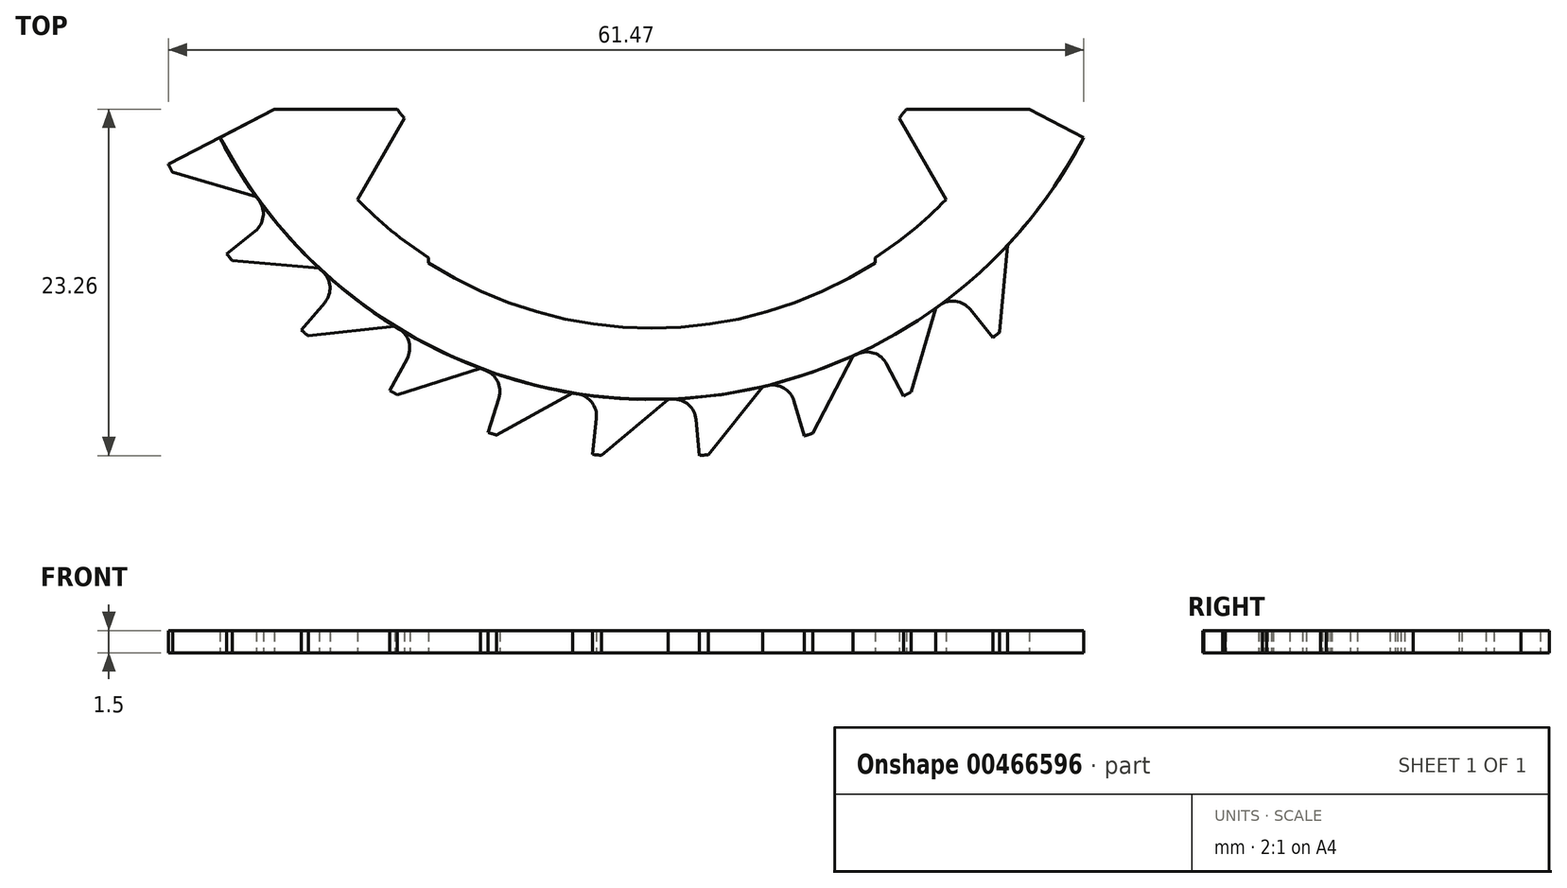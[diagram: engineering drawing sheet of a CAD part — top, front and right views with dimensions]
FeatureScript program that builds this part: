
annotation { "Feature Type Name" : "Feature", "Feature Type Description" : "" }
export const myFeature = defineFeature(function(context is Context, id is Id, definition is map)
    precondition{}
    {
        {
            var Q0;
            Q0=qCreatedBy(makeId("Top.planeOp"),FACE);
            var sketch = newSketch(context, id + "F0", { "sketchPlane" : qUnion([Q0])});
            skArc(sketch, "E0", {"start": v(5, -7.72) * mm, "mid": v(5.83, -7.12) * mm, "end": v(6.6, -6.42) * mm});
            skArc(sketch, "E1", {"start": v(-5, -7.84) * mm, "mid": v(0, -9.3) * mm, "end": v(5, -7.84) * mm});
            skArc(sketch, "E2", {"start": v(7.64, -9.51) * mm, "mid": v(7.71, -9.45) * mm, "end": v(7.8, -9.39) * mm});
            skCircle(sketch, "E3", {"center": v(0, 0) * mm, "radius": 10.9 * mm});
            skLineSegment(sketch, "E4", {"start": v(0, 0) * mm, "end": v(-10.82, -5.63) * mm});
            skLineSegment(sketch, "E5", {"start": v(0, 0) * mm, "end": v(9.67, -5.03) * mm});
            skLineSegment(sketch, "E6", {"start": v(0, 0) * mm, "end": v(7.64, -9.51) * mm, "construction": true});
            skLineSegment(sketch, "E7", {"start": v(6.82, -8.5) * mm, "end": v(7.64, -9.51) * mm});
            skLineSegment(sketch, "E8", {"start": v(7.8, -9.39) * mm, "end": v(7.96, -7.45) * mm});
            skLineSegment(sketch, "E9", {"start": v(0, 0) * mm, "end": v(9.35, -7.84) * mm, "construction": true});
            skLineSegment(sketch, "E10.1.0", {"start": v(5.8, -10.73) * mm, "end": v(6.36, -8.86) * mm});
            skArc(sketch, "E10.1.1", {"start": v(5.63, -10.82) * mm, "mid": v(5.72, -10.77) * mm, "end": v(5.8, -10.73) * mm});
            skLineSegment(sketch, "E10.1.2", {"start": v(5.03, -9.67) * mm, "end": v(5.63, -10.82) * mm});
            skLineSegment(sketch, "E10.2.0", {"start": v(3.6, -11.66) * mm, "end": v(4.5, -9.92) * mm});
            skArc(sketch, "E10.2.1", {"start": v(3.41, -11.71) * mm, "mid": v(3.5, -11.68) * mm, "end": v(3.6, -11.66) * mm});
            skLineSegment(sketch, "E10.2.2", {"start": v(3.05, -10.46) * mm, "end": v(3.41, -11.71) * mm});
            skLineSegment(sketch, "E10.3.0", {"start": v(1.26, -12.13) * mm, "end": v(2.48, -10.61) * mm});
            skArc(sketch, "E10.3.1", {"start": v(1.06, -12.15) * mm, "mid": v(1.16, -12.14) * mm, "end": v(1.26, -12.13) * mm});
            skLineSegment(sketch, "E10.3.2", {"start": v(0.95, -10.86) * mm, "end": v(1.06, -12.15) * mm});
            skLineSegment(sketch, "E10.4.0", {"start": v(-1.13, -12.15) * mm, "end": v(0.36, -10.9) * mm});
            skArc(sketch, "E10.4.1", {"start": v(-1.33, -12.13) * mm, "mid": v(-1.23, -12.14) * mm, "end": v(-1.13, -12.15) * mm});
            skLineSegment(sketch, "E10.4.2", {"start": v(-1.19, -10.84) * mm, "end": v(-1.33, -12.13) * mm});
            skLineSegment(sketch, "E10.5.0", {"start": v(-3.48, -11.7) * mm, "end": v(-1.77, -10.76) * mm});
            skArc(sketch, "E10.5.1", {"start": v(-3.67, -11.64) * mm, "mid": v(-3.57, -11.67) * mm, "end": v(-3.48, -11.7) * mm});
            skLineSegment(sketch, "E10.5.2", {"start": v(-3.28, -10.4) * mm, "end": v(-3.67, -11.64) * mm});
            skLineSegment(sketch, "E10.6.0", {"start": v(-5.7, -10.8) * mm, "end": v(-3.83, -10.2) * mm});
            skArc(sketch, "E10.6.1", {"start": v(-5.87, -10.7) * mm, "mid": v(-5.78, -10.74) * mm, "end": v(-5.7, -10.8) * mm});
            skLineSegment(sketch, "E10.6.2", {"start": v(-5.24, -9.56) * mm, "end": v(-5.87, -10.7) * mm});
            skLineSegment(sketch, "E10.7.0", {"start": v(-7.69, -9.47) * mm, "end": v(-5.75, -9.26) * mm});
            skArc(sketch, "E10.7.1", {"start": v(-7.84, -9.35) * mm, "mid": v(-7.77, -9.4) * mm, "end": v(-7.69, -9.47) * mm});
            skLineSegment(sketch, "E10.7.2", {"start": v(-7, -8.35) * mm, "end": v(-7.84, -9.35) * mm});
            skLineSegment(sketch, "E10.8.0", {"start": v(-9.39, -7.8) * mm, "end": v(-7.45, -7.96) * mm});
            skArc(sketch, "E10.8.1", {"start": v(-9.51, -7.64) * mm, "mid": v(-9.45, -7.71) * mm, "end": v(-9.39, -7.8) * mm});
            skLineSegment(sketch, "E10.8.2", {"start": v(-8.5, -6.82) * mm, "end": v(-9.51, -7.64) * mm});
            skLineSegment(sketch, "E10.9.0", {"start": v(-10.73, -5.8) * mm, "end": v(-8.86, -6.36) * mm});
            skArc(sketch, "E10.9.1", {"start": v(-10.82, -5.63) * mm, "mid": v(-10.77, -5.72) * mm, "end": v(-10.73, -5.8) * mm});
            skLineSegment(sketch, "E10.9.2", {"start": v(-9.67, -5.03) * mm, "end": v(-10.82, -5.63) * mm});
            skLineSegment(sketch, "E10.anchor1", {"start": v(0, 0) * mm, "end": v(7.8, -9.39) * mm, "construction": true});
            skLineSegment(sketch, "E10.anchor2", {"start": v(0, 0) * mm, "end": v(-9.58, -5.2) * mm, "construction": true});
            skArc(sketch, "E11", {"start": v(7.13, -8.88) * mm, "mid": v(6.8, -8.7) * mm, "end": v(6.44, -8.8) * mm});
            skArc(sketch, "E12.1.0", {"start": v(5.26, -10.1) * mm, "mid": v(4.98, -9.86) * mm, "end": v(4.6, -9.88) * mm});
            skArc(sketch, "E12.2.0", {"start": v(3.19, -10.93) * mm, "mid": v(2.96, -10.64) * mm, "end": v(2.59, -10.59) * mm});
            skArc(sketch, "E12.3.0", {"start": v(1, -11.35) * mm, "mid": v(0.82, -11.01) * mm, "end": v(0.47, -10.89) * mm});
            skArc(sketch, "E12.4.0", {"start": v(-1.24, -11.32) * mm, "mid": v(-1.34, -10.96) * mm, "end": v(-1.66, -10.77) * mm});
            skArc(sketch, "E12.5.0", {"start": v(-3.42, -10.86) * mm, "mid": v(-3.45, -10.5) * mm, "end": v(-3.73, -10.24) * mm});
            skArc(sketch, "E12.6.0", {"start": v(-5.48, -9.99) * mm, "mid": v(-5.43, -9.62) * mm, "end": v(-5.66, -9.32) * mm});
            skArc(sketch, "E12.7.0", {"start": v(-7.32, -8.72) * mm, "mid": v(-7.2, -8.37) * mm, "end": v(-7.37, -8.03) * mm});
            skArc(sketch, "E12.8.0", {"start": v(-8.88, -7.13) * mm, "mid": v(-8.7, -6.8) * mm, "end": v(-8.8, -6.44) * mm});
            skLineSegment(sketch, "E12.anchor1", {"start": v(6.44, -8.8) * mm, "end": v(0, 0) * mm, "construction": true});
            skLineSegment(sketch, "E12.anchor2", {"start": v(0, 0) * mm, "end": v(-8.8, -6.44) * mm, "construction": true});
            skCircle(sketch, "E13", {"center": v(0, 0) * mm, "radius": 12.2 * mm, "construction": true});
            skLineSegment(sketch, "E14", {"start": v(-8.45, -4.4) * mm, "end": v(-5.7, -4.4) * mm});
            skPoint(sketch, "E15", {"position": v(0, 5) * mm});
            skLineSegment(sketch, "E16", {"start": v(0, 5) * mm, "end": v(-6.6, -6.42) * mm});
            skLineSegment(sketch, "E17", {"start": v(0, 5) * mm, "end": v(6.6, -6.42) * mm});
            skLineSegment(sketch, "E18", {"start": v(-5, -7.72) * mm, "end": v(-5, -7.84) * mm});
            skLineSegment(sketch, "E19", {"start": v(5, -7.72) * mm, "end": v(5, -7.84) * mm});
            skArc(sketch, "E20.trimOffspring", {"start": v(5.52, -4.63) * mm, "mid": v(5.6, -4.51) * mm, "end": v(5.7, -4.4) * mm});
            skLineSegment(sketch, "E21.trimOffspring", {"start": v(5.7, -4.4) * mm, "end": v(8.45, -4.4) * mm});
            skLineSegment(sketch, "E22.trimOffspring", {"start": v(-9.58, -5.2) * mm, "end": v(-10.73, -5.8) * mm, "construction": true});
            skArc(sketch, "E23", {"start": v(-5.7, -4.4) * mm, "mid": v(-5.62, -4.5) * mm, "end": v(-5.54, -4.6) * mm});
            skArc(sketch, "E24", {"start": v(-6.6, -6.42) * mm, "mid": v(-5.83, -7.12) * mm, "end": v(-5, -7.72) * mm});
            skSolve(sketch);
        }
        {
            var Q0;
            {var subQ6=sQuery(id+"F0.wireOp",EDGE,"E0");Q0=makeQuery(id+"F0.imprint","IMPRINT",FACE,{"disambiguationData":[TD([[makeQuery(id+"F0.imprint","IMPRINT",EDGE,{"derivedFrom":subQ6}),-1.0]])]});}
            var Q1;
            {var subQ1=sQuery(id+"F0.wireOp",EDGE,"E10.9.0");Q1=makeQuery(id+"F0.imprint","IMPRINT",FACE,{"disambiguationData":[TD([[makeQuery(id+"F0.imprint","IMPRINT",EDGE,{"derivedFrom":subQ1}),1.0]])]});}
            var Q2;
            {var subQ5=sQuery(id+"F0.wireOp",EDGE,"E10.8.0");Q2=makeQuery(id+"F0.imprint","IMPRINT",FACE,{"disambiguationData":[TD([[makeQuery(id+"F0.imprint","IMPRINT",EDGE,{"derivedFrom":subQ5}),1.0]])]});}
            var Q3;
            {var subQ5=sQuery(id+"F0.wireOp",EDGE,"E10.7.0");Q3=makeQuery(id+"F0.imprint","IMPRINT",FACE,{"disambiguationData":[TD([[makeQuery(id+"F0.imprint","IMPRINT",EDGE,{"derivedFrom":subQ5}),1.0]])]});}
            var Q4;
            {var subQ5=sQuery(id+"F0.wireOp",EDGE,"E10.6.0");Q4=makeQuery(id+"F0.imprint","IMPRINT",FACE,{"disambiguationData":[TD([[makeQuery(id+"F0.imprint","IMPRINT",EDGE,{"derivedFrom":subQ5}),1.0]])]});}
            var Q5;
            {var subQ5=sQuery(id+"F0.wireOp",EDGE,"E10.5.0");Q5=makeQuery(id+"F0.imprint","IMPRINT",FACE,{"disambiguationData":[TD([[makeQuery(id+"F0.imprint","IMPRINT",EDGE,{"derivedFrom":subQ5}),1.0]])]});}
            var Q6;
            {var subQ5=sQuery(id+"F0.wireOp",EDGE,"E10.4.0");Q6=makeQuery(id+"F0.imprint","IMPRINT",FACE,{"disambiguationData":[TD([[makeQuery(id+"F0.imprint","IMPRINT",EDGE,{"derivedFrom":subQ5}),1.0]])]});}
            var Q7;
            {var subQ5=sQuery(id+"F0.wireOp",EDGE,"E10.3.0");Q7=makeQuery(id+"F0.imprint","IMPRINT",FACE,{"disambiguationData":[TD([[makeQuery(id+"F0.imprint","IMPRINT",EDGE,{"derivedFrom":subQ5}),1.0]])]});}
            var Q8;
            {var subQ2=sQuery(id+"F0.wireOp",EDGE,"E2");Q8=makeQuery(id+"F0.imprint","IMPRINT",FACE,{"disambiguationData":[TD([[makeQuery(id+"F0.imprint","IMPRINT",EDGE,{"derivedFrom":subQ2}),1.0]])]});}
            var Q9;
            {var subQ5=sQuery(id+"F0.wireOp",EDGE,"E10.1.0");Q9=makeQuery(id+"F0.imprint","IMPRINT",FACE,{"disambiguationData":[TD([[makeQuery(id+"F0.imprint","IMPRINT",EDGE,{"derivedFrom":subQ5}),1.0]])]});}
            var Q10;
            {var subQ5=sQuery(id+"F0.wireOp",EDGE,"E10.2.0");Q10=makeQuery(id+"F0.imprint","IMPRINT",FACE,{"disambiguationData":[TD([[makeQuery(id+"F0.imprint","IMPRINT",EDGE,{"derivedFrom":subQ5}),1.0]])]});}
            var Q11;
            {var subQ1=sQuery(id+"F0.wireOp",EDGE,"E11");Q11=makeQuery(id+"F0.imprint","IMPRINT",FACE,{"disambiguationData":[TD([[makeQuery(id+"F0.imprint","IMPRINT",EDGE,{"derivedFrom":subQ1}),-1.0]])]});}
            var Q12;
            {var subQ0=sQuery(id+"F0.wireOp",EDGE,"E12.1.0");Q12=makeQuery(id+"F0.imprint","IMPRINT",FACE,{"disambiguationData":[TD([[makeQuery(id+"F0.imprint","IMPRINT",EDGE,{"derivedFrom":subQ0}),-1.0]])]});}
            var Q13;
            {var subQ0=sQuery(id+"F0.wireOp",EDGE,"E12.2.0");Q13=makeQuery(id+"F0.imprint","IMPRINT",FACE,{"disambiguationData":[TD([[makeQuery(id+"F0.imprint","IMPRINT",EDGE,{"derivedFrom":subQ0}),-1.0]])]});}
            var Q14;
            {var subQ0=sQuery(id+"F0.wireOp",EDGE,"E12.3.0");Q14=makeQuery(id+"F0.imprint","IMPRINT",FACE,{"disambiguationData":[TD([[makeQuery(id+"F0.imprint","IMPRINT",EDGE,{"derivedFrom":subQ0}),-1.0]])]});}
            var Q15;
            {var subQ0=sQuery(id+"F0.wireOp",EDGE,"E12.4.0");Q15=makeQuery(id+"F0.imprint","IMPRINT",FACE,{"disambiguationData":[TD([[makeQuery(id+"F0.imprint","IMPRINT",EDGE,{"derivedFrom":subQ0}),-1.0]])]});}
            var Q16;
            {var subQ0=sQuery(id+"F0.wireOp",EDGE,"E12.5.0");Q16=makeQuery(id+"F0.imprint","IMPRINT",FACE,{"disambiguationData":[TD([[makeQuery(id+"F0.imprint","IMPRINT",EDGE,{"derivedFrom":subQ0}),-1.0]])]});}
            var Q17;
            {var subQ0=sQuery(id+"F0.wireOp",EDGE,"E12.6.0");Q17=makeQuery(id+"F0.imprint","IMPRINT",FACE,{"disambiguationData":[TD([[makeQuery(id+"F0.imprint","IMPRINT",EDGE,{"derivedFrom":subQ0}),-1.0]])]});}
            var Q18;
            {var subQ0=sQuery(id+"F0.wireOp",EDGE,"E12.8.0");Q18=makeQuery(id+"F0.imprint","IMPRINT",FACE,{"disambiguationData":[TD([[makeQuery(id+"F0.imprint","IMPRINT",EDGE,{"derivedFrom":subQ0}),-1.0]])]});}
            var Q19;
            {var subQ0=sQuery(id+"F0.wireOp",EDGE,"E12.7.0");Q19=makeQuery(id+"F0.imprint","IMPRINT",FACE,{"disambiguationData":[TD([[makeQuery(id+"F0.imprint","IMPRINT",EDGE,{"derivedFrom":subQ0}),-1.0]])]});}
            extrude(context, id + "F1", {"entities" : qUnion([Q0, Q1, Q2, Q3, Q4, Q5, Q6, Q7, Q8, Q9, Q10, Q11, Q12, Q13, Q14, Q15, Q16, Q17, Q18, Q19]), "depth" : 0.5 * mm});
        }
        {
            var Q0;
            {var subQ6=sQuery(id+"F0.wireOp",EDGE,"E0");Q0=makeQuery(id+"F0.imprint","IMPRINT",FACE,{"disambiguationData":[TD([[makeQuery(id+"F0.imprint","IMPRINT",EDGE,{"derivedFrom":subQ6}),-1.0]])]});}
            var Q1;
            {var subQ2=sQuery(id+"F0.wireOp",EDGE,"E2");Q1=makeQuery(id+"F0.imprint","IMPRINT",FACE,{"disambiguationData":[TD([[makeQuery(id+"F0.imprint","IMPRINT",EDGE,{"derivedFrom":subQ2}),1.0]])]});}
            var Q2;
            {var subQ1=sQuery(id+"F0.wireOp",EDGE,"E11");Q2=makeQuery(id+"F0.imprint","IMPRINT",FACE,{"disambiguationData":[TD([[makeQuery(id+"F0.imprint","IMPRINT",EDGE,{"derivedFrom":subQ1}),-1.0]])]});}
            var Q3;
            {var subQ5=sQuery(id+"F0.wireOp",EDGE,"E10.1.0");Q3=makeQuery(id+"F0.imprint","IMPRINT",FACE,{"disambiguationData":[TD([[makeQuery(id+"F0.imprint","IMPRINT",EDGE,{"derivedFrom":subQ5}),1.0]])]});}
            var Q4;
            {var subQ0=sQuery(id+"F0.wireOp",EDGE,"E12.1.0");Q4=makeQuery(id+"F0.imprint","IMPRINT",FACE,{"disambiguationData":[TD([[makeQuery(id+"F0.imprint","IMPRINT",EDGE,{"derivedFrom":subQ0}),-1.0]])]});}
            var Q5;
            {var subQ5=sQuery(id+"F0.wireOp",EDGE,"E10.2.0");Q5=makeQuery(id+"F0.imprint","IMPRINT",FACE,{"disambiguationData":[TD([[makeQuery(id+"F0.imprint","IMPRINT",EDGE,{"derivedFrom":subQ5}),1.0]])]});}
            var Q6;
            {var subQ0=sQuery(id+"F0.wireOp",EDGE,"E12.2.0");Q6=makeQuery(id+"F0.imprint","IMPRINT",FACE,{"disambiguationData":[TD([[makeQuery(id+"F0.imprint","IMPRINT",EDGE,{"derivedFrom":subQ0}),-1.0]])]});}
            var Q7;
            {var subQ5=sQuery(id+"F0.wireOp",EDGE,"E10.3.0");Q7=makeQuery(id+"F0.imprint","IMPRINT",FACE,{"disambiguationData":[TD([[makeQuery(id+"F0.imprint","IMPRINT",EDGE,{"derivedFrom":subQ5}),1.0]])]});}
            var Q8;
            {var subQ0=sQuery(id+"F0.wireOp",EDGE,"E12.3.0");Q8=makeQuery(id+"F0.imprint","IMPRINT",FACE,{"disambiguationData":[TD([[makeQuery(id+"F0.imprint","IMPRINT",EDGE,{"derivedFrom":subQ0}),-1.0]])]});}
            var Q9;
            {var subQ5=sQuery(id+"F0.wireOp",EDGE,"E10.4.0");Q9=makeQuery(id+"F0.imprint","IMPRINT",FACE,{"disambiguationData":[TD([[makeQuery(id+"F0.imprint","IMPRINT",EDGE,{"derivedFrom":subQ5}),1.0]])]});}
            var Q10;
            {var subQ0=sQuery(id+"F0.wireOp",EDGE,"E12.4.0");Q10=makeQuery(id+"F0.imprint","IMPRINT",FACE,{"disambiguationData":[TD([[makeQuery(id+"F0.imprint","IMPRINT",EDGE,{"derivedFrom":subQ0}),-1.0]])]});}
            var Q11;
            {var subQ5=sQuery(id+"F0.wireOp",EDGE,"E10.5.0");Q11=makeQuery(id+"F0.imprint","IMPRINT",FACE,{"disambiguationData":[TD([[makeQuery(id+"F0.imprint","IMPRINT",EDGE,{"derivedFrom":subQ5}),1.0]])]});}
            var Q12;
            {var subQ0=sQuery(id+"F0.wireOp",EDGE,"E12.5.0");Q12=makeQuery(id+"F0.imprint","IMPRINT",FACE,{"disambiguationData":[TD([[makeQuery(id+"F0.imprint","IMPRINT",EDGE,{"derivedFrom":subQ0}),-1.0]])]});}
            var Q13;
            {var subQ5=sQuery(id+"F0.wireOp",EDGE,"E10.6.0");Q13=makeQuery(id+"F0.imprint","IMPRINT",FACE,{"disambiguationData":[TD([[makeQuery(id+"F0.imprint","IMPRINT",EDGE,{"derivedFrom":subQ5}),1.0]])]});}
            var Q14;
            {var subQ0=sQuery(id+"F0.wireOp",EDGE,"E12.6.0");Q14=makeQuery(id+"F0.imprint","IMPRINT",FACE,{"disambiguationData":[TD([[makeQuery(id+"F0.imprint","IMPRINT",EDGE,{"derivedFrom":subQ0}),-1.0]])]});}
            var Q15;
            {var subQ5=sQuery(id+"F0.wireOp",EDGE,"E10.7.0");Q15=makeQuery(id+"F0.imprint","IMPRINT",FACE,{"disambiguationData":[TD([[makeQuery(id+"F0.imprint","IMPRINT",EDGE,{"derivedFrom":subQ5}),1.0]])]});}
            var Q16;
            {var subQ0=sQuery(id+"F0.wireOp",EDGE,"E12.7.0");Q16=makeQuery(id+"F0.imprint","IMPRINT",FACE,{"disambiguationData":[TD([[makeQuery(id+"F0.imprint","IMPRINT",EDGE,{"derivedFrom":subQ0}),-1.0]])]});}
            var Q17;
            {var subQ5=sQuery(id+"F0.wireOp",EDGE,"E10.8.0");Q17=makeQuery(id+"F0.imprint","IMPRINT",FACE,{"disambiguationData":[TD([[makeQuery(id+"F0.imprint","IMPRINT",EDGE,{"derivedFrom":subQ5}),1.0]])]});}
            var Q18;
            {var subQ0=sQuery(id+"F0.wireOp",EDGE,"E12.8.0");Q18=makeQuery(id+"F0.imprint","IMPRINT",FACE,{"disambiguationData":[TD([[makeQuery(id+"F0.imprint","IMPRINT",EDGE,{"derivedFrom":subQ0}),-1.0]])]});}
            extrude(context, id + "F2", {"entities" : qUnion([Q0, Q1, Q2, Q3, Q4, Q5, Q6, Q7, Q8, Q9, Q10, Q11, Q12, Q13, Q14, Q15, Q16, Q17, Q18]), "depth" : 0.5 * mm});
        }
        {
            var Q0;
            {var subQ6=sQuery(id+"F0.wireOp",EDGE,"E0");Q0=makeQuery(id+"F0.imprint","IMPRINT",FACE,{"disambiguationData":[TD([[makeQuery(id+"F0.imprint","IMPRINT",EDGE,{"derivedFrom":subQ6}),-1.0]])]});}
            var Q1;
            {var subQ5=sQuery(id+"F0.wireOp",EDGE,"E10.7.0");Q1=makeQuery(id+"F0.imprint","IMPRINT",FACE,{"disambiguationData":[TD([[makeQuery(id+"F0.imprint","IMPRINT",EDGE,{"derivedFrom":subQ5}),1.0]])]});}
            var Q2;
            {var subQ0=sQuery(id+"F0.wireOp",EDGE,"E12.6.0");Q2=makeQuery(id+"F0.imprint","IMPRINT",FACE,{"disambiguationData":[TD([[makeQuery(id+"F0.imprint","IMPRINT",EDGE,{"derivedFrom":subQ0}),-1.0]])]});}
            var Q3;
            {var subQ5=sQuery(id+"F0.wireOp",EDGE,"E10.6.0");Q3=makeQuery(id+"F0.imprint","IMPRINT",FACE,{"disambiguationData":[TD([[makeQuery(id+"F0.imprint","IMPRINT",EDGE,{"derivedFrom":subQ5}),1.0]])]});}
            var Q4;
            {var subQ0=sQuery(id+"F0.wireOp",EDGE,"E12.5.0");Q4=makeQuery(id+"F0.imprint","IMPRINT",FACE,{"disambiguationData":[TD([[makeQuery(id+"F0.imprint","IMPRINT",EDGE,{"derivedFrom":subQ0}),-1.0]])]});}
            var Q5;
            {var subQ5=sQuery(id+"F0.wireOp",EDGE,"E10.5.0");Q5=makeQuery(id+"F0.imprint","IMPRINT",FACE,{"disambiguationData":[TD([[makeQuery(id+"F0.imprint","IMPRINT",EDGE,{"derivedFrom":subQ5}),1.0]])]});}
            var Q6;
            {var subQ0=sQuery(id+"F0.wireOp",EDGE,"E12.4.0");Q6=makeQuery(id+"F0.imprint","IMPRINT",FACE,{"disambiguationData":[TD([[makeQuery(id+"F0.imprint","IMPRINT",EDGE,{"derivedFrom":subQ0}),-1.0]])]});}
            var Q7;
            {var subQ5=sQuery(id+"F0.wireOp",EDGE,"E10.4.0");Q7=makeQuery(id+"F0.imprint","IMPRINT",FACE,{"disambiguationData":[TD([[makeQuery(id+"F0.imprint","IMPRINT",EDGE,{"derivedFrom":subQ5}),1.0]])]});}
            var Q8;
            {var subQ0=sQuery(id+"F0.wireOp",EDGE,"E12.3.0");Q8=makeQuery(id+"F0.imprint","IMPRINT",FACE,{"disambiguationData":[TD([[makeQuery(id+"F0.imprint","IMPRINT",EDGE,{"derivedFrom":subQ0}),-1.0]])]});}
            var Q9;
            {var subQ5=sQuery(id+"F0.wireOp",EDGE,"E10.3.0");Q9=makeQuery(id+"F0.imprint","IMPRINT",FACE,{"disambiguationData":[TD([[makeQuery(id+"F0.imprint","IMPRINT",EDGE,{"derivedFrom":subQ5}),1.0]])]});}
            var Q10;
            {var subQ0=sQuery(id+"F0.wireOp",EDGE,"E12.2.0");Q10=makeQuery(id+"F0.imprint","IMPRINT",FACE,{"disambiguationData":[TD([[makeQuery(id+"F0.imprint","IMPRINT",EDGE,{"derivedFrom":subQ0}),-1.0]])]});}
            var Q11;
            {var subQ5=sQuery(id+"F0.wireOp",EDGE,"E10.2.0");Q11=makeQuery(id+"F0.imprint","IMPRINT",FACE,{"disambiguationData":[TD([[makeQuery(id+"F0.imprint","IMPRINT",EDGE,{"derivedFrom":subQ5}),1.0]])]});}
            var Q12;
            {var subQ0=sQuery(id+"F0.wireOp",EDGE,"E12.1.0");Q12=makeQuery(id+"F0.imprint","IMPRINT",FACE,{"disambiguationData":[TD([[makeQuery(id+"F0.imprint","IMPRINT",EDGE,{"derivedFrom":subQ0}),-1.0]])]});}
            var Q13;
            {var subQ5=sQuery(id+"F0.wireOp",EDGE,"E10.1.0");Q13=makeQuery(id+"F0.imprint","IMPRINT",FACE,{"disambiguationData":[TD([[makeQuery(id+"F0.imprint","IMPRINT",EDGE,{"derivedFrom":subQ5}),1.0]])]});}
            var Q14;
            {var subQ2=sQuery(id+"F0.wireOp",EDGE,"E2");Q14=makeQuery(id+"F0.imprint","IMPRINT",FACE,{"disambiguationData":[TD([[makeQuery(id+"F0.imprint","IMPRINT",EDGE,{"derivedFrom":subQ2}),1.0]])]});}
            var Q15;
            {var subQ1=sQuery(id+"F0.wireOp",EDGE,"E11");Q15=makeQuery(id+"F0.imprint","IMPRINT",FACE,{"disambiguationData":[TD([[makeQuery(id+"F0.imprint","IMPRINT",EDGE,{"derivedFrom":subQ1}),-1.0]])]});}
            var Q16;
            {var subQ0=sQuery(id+"F0.wireOp",EDGE,"E12.7.0");Q16=makeQuery(id+"F0.imprint","IMPRINT",FACE,{"disambiguationData":[TD([[makeQuery(id+"F0.imprint","IMPRINT",EDGE,{"derivedFrom":subQ0}),-1.0]])]});}
            extrude(context, id + "F3", {"entities" : qUnion([Q0, Q1, Q2, Q3, Q4, Q5, Q6, Q7, Q8, Q9, Q10, Q11, Q12, Q13, Q14, Q15, Q16]), "depth" : 0.5 * mm});
        }
        {
            var Q0;
            {var subQ2=sQuery(id+"F0.wireOp",EDGE,"E2");Q0=makeQuery(id+"F0.imprint","IMPRINT",FACE,{"disambiguationData":[TD([[makeQuery(id+"F0.imprint","IMPRINT",EDGE,{"derivedFrom":subQ2}),1.0]])]});}
            var Q1;
            {var subQ1=sQuery(id+"F0.wireOp",EDGE,"E11");Q1=makeQuery(id+"F0.imprint","IMPRINT",FACE,{"disambiguationData":[TD([[makeQuery(id+"F0.imprint","IMPRINT",EDGE,{"derivedFrom":subQ1}),-1.0]])]});}
            var Q2;
            {var subQ5=sQuery(id+"F0.wireOp",EDGE,"E10.1.0");Q2=makeQuery(id+"F0.imprint","IMPRINT",FACE,{"disambiguationData":[TD([[makeQuery(id+"F0.imprint","IMPRINT",EDGE,{"derivedFrom":subQ5}),1.0]])]});}
            var Q3;
            {var subQ0=sQuery(id+"F0.wireOp",EDGE,"E12.1.0");Q3=makeQuery(id+"F0.imprint","IMPRINT",FACE,{"disambiguationData":[TD([[makeQuery(id+"F0.imprint","IMPRINT",EDGE,{"derivedFrom":subQ0}),-1.0]])]});}
            var Q4;
            {var subQ5=sQuery(id+"F0.wireOp",EDGE,"E10.2.0");Q4=makeQuery(id+"F0.imprint","IMPRINT",FACE,{"disambiguationData":[TD([[makeQuery(id+"F0.imprint","IMPRINT",EDGE,{"derivedFrom":subQ5}),1.0]])]});}
            var Q5;
            {var subQ0=sQuery(id+"F0.wireOp",EDGE,"E12.2.0");Q5=makeQuery(id+"F0.imprint","IMPRINT",FACE,{"disambiguationData":[TD([[makeQuery(id+"F0.imprint","IMPRINT",EDGE,{"derivedFrom":subQ0}),-1.0]])]});}
            var Q6;
            {var subQ5=sQuery(id+"F0.wireOp",EDGE,"E10.3.0");Q6=makeQuery(id+"F0.imprint","IMPRINT",FACE,{"disambiguationData":[TD([[makeQuery(id+"F0.imprint","IMPRINT",EDGE,{"derivedFrom":subQ5}),1.0]])]});}
            var Q7;
            {var subQ0=sQuery(id+"F0.wireOp",EDGE,"E12.3.0");Q7=makeQuery(id+"F0.imprint","IMPRINT",FACE,{"disambiguationData":[TD([[makeQuery(id+"F0.imprint","IMPRINT",EDGE,{"derivedFrom":subQ0}),-1.0]])]});}
            var Q8;
            {var subQ5=sQuery(id+"F0.wireOp",EDGE,"E10.4.0");Q8=makeQuery(id+"F0.imprint","IMPRINT",FACE,{"disambiguationData":[TD([[makeQuery(id+"F0.imprint","IMPRINT",EDGE,{"derivedFrom":subQ5}),1.0]])]});}
            var Q9;
            {var subQ0=sQuery(id+"F0.wireOp",EDGE,"E12.4.0");Q9=makeQuery(id+"F0.imprint","IMPRINT",FACE,{"disambiguationData":[TD([[makeQuery(id+"F0.imprint","IMPRINT",EDGE,{"derivedFrom":subQ0}),-1.0]])]});}
            var Q10;
            {var subQ5=sQuery(id+"F0.wireOp",EDGE,"E10.5.0");Q10=makeQuery(id+"F0.imprint","IMPRINT",FACE,{"disambiguationData":[TD([[makeQuery(id+"F0.imprint","IMPRINT",EDGE,{"derivedFrom":subQ5}),1.0]])]});}
            var Q11;
            {var subQ0=sQuery(id+"F0.wireOp",EDGE,"E12.5.0");Q11=makeQuery(id+"F0.imprint","IMPRINT",FACE,{"disambiguationData":[TD([[makeQuery(id+"F0.imprint","IMPRINT",EDGE,{"derivedFrom":subQ0}),-1.0]])]});}
            var Q12;
            {var subQ5=sQuery(id+"F0.wireOp",EDGE,"E10.6.0");Q12=makeQuery(id+"F0.imprint","IMPRINT",FACE,{"disambiguationData":[TD([[makeQuery(id+"F0.imprint","IMPRINT",EDGE,{"derivedFrom":subQ5}),1.0]])]});}
            var Q13;
            {var subQ6=sQuery(id+"F0.wireOp",EDGE,"E0");Q13=makeQuery(id+"F0.imprint","IMPRINT",FACE,{"disambiguationData":[TD([[makeQuery(id+"F0.imprint","IMPRINT",EDGE,{"derivedFrom":subQ6}),-1.0]])]});}
            var Q14;
            {var subQ0=sQuery(id+"F0.wireOp",EDGE,"E12.6.0");Q14=makeQuery(id+"F0.imprint","IMPRINT",FACE,{"disambiguationData":[TD([[makeQuery(id+"F0.imprint","IMPRINT",EDGE,{"derivedFrom":subQ0}),-1.0]])]});}
            extrude(context, id + "F4", {"entities" : qUnion([Q0, Q1, Q2, Q3, Q4, Q5, Q6, Q7, Q8, Q9, Q10, Q11, Q12, Q13, Q14]), "depth" : 0.5 * mm});
        }
        {
            var Q0;
            {var subQ6=sQuery(id+"F0.wireOp",EDGE,"E0");Q0=makeQuery(id+"F0.imprint","IMPRINT",FACE,{"disambiguationData":[TD([[makeQuery(id+"F0.imprint","IMPRINT",EDGE,{"derivedFrom":subQ6}),-1.0]])]});}
            var Q1;
            {var subQ5=sQuery(id+"F0.wireOp",EDGE,"E10.5.0");Q1=makeQuery(id+"F0.imprint","IMPRINT",FACE,{"disambiguationData":[TD([[makeQuery(id+"F0.imprint","IMPRINT",EDGE,{"derivedFrom":subQ5}),1.0]])]});}
            var Q2;
            {var subQ0=sQuery(id+"F0.wireOp",EDGE,"E12.4.0");Q2=makeQuery(id+"F0.imprint","IMPRINT",FACE,{"disambiguationData":[TD([[makeQuery(id+"F0.imprint","IMPRINT",EDGE,{"derivedFrom":subQ0}),-1.0]])]});}
            var Q3;
            {var subQ5=sQuery(id+"F0.wireOp",EDGE,"E10.4.0");Q3=makeQuery(id+"F0.imprint","IMPRINT",FACE,{"disambiguationData":[TD([[makeQuery(id+"F0.imprint","IMPRINT",EDGE,{"derivedFrom":subQ5}),1.0]])]});}
            var Q4;
            {var subQ0=sQuery(id+"F0.wireOp",EDGE,"E12.3.0");Q4=makeQuery(id+"F0.imprint","IMPRINT",FACE,{"disambiguationData":[TD([[makeQuery(id+"F0.imprint","IMPRINT",EDGE,{"derivedFrom":subQ0}),-1.0]])]});}
            var Q5;
            {var subQ5=sQuery(id+"F0.wireOp",EDGE,"E10.3.0");Q5=makeQuery(id+"F0.imprint","IMPRINT",FACE,{"disambiguationData":[TD([[makeQuery(id+"F0.imprint","IMPRINT",EDGE,{"derivedFrom":subQ5}),1.0]])]});}
            var Q6;
            {var subQ0=sQuery(id+"F0.wireOp",EDGE,"E12.2.0");Q6=makeQuery(id+"F0.imprint","IMPRINT",FACE,{"disambiguationData":[TD([[makeQuery(id+"F0.imprint","IMPRINT",EDGE,{"derivedFrom":subQ0}),-1.0]])]});}
            var Q7;
            {var subQ5=sQuery(id+"F0.wireOp",EDGE,"E10.2.0");Q7=makeQuery(id+"F0.imprint","IMPRINT",FACE,{"disambiguationData":[TD([[makeQuery(id+"F0.imprint","IMPRINT",EDGE,{"derivedFrom":subQ5}),1.0]])]});}
            var Q8;
            {var subQ0=sQuery(id+"F0.wireOp",EDGE,"E12.1.0");Q8=makeQuery(id+"F0.imprint","IMPRINT",FACE,{"disambiguationData":[TD([[makeQuery(id+"F0.imprint","IMPRINT",EDGE,{"derivedFrom":subQ0}),-1.0]])]});}
            var Q9;
            {var subQ5=sQuery(id+"F0.wireOp",EDGE,"E10.1.0");Q9=makeQuery(id+"F0.imprint","IMPRINT",FACE,{"disambiguationData":[TD([[makeQuery(id+"F0.imprint","IMPRINT",EDGE,{"derivedFrom":subQ5}),1.0]])]});}
            var Q10;
            {var subQ1=sQuery(id+"F0.wireOp",EDGE,"E11");Q10=makeQuery(id+"F0.imprint","IMPRINT",FACE,{"disambiguationData":[TD([[makeQuery(id+"F0.imprint","IMPRINT",EDGE,{"derivedFrom":subQ1}),-1.0]])]});}
            var Q11;
            {var subQ2=sQuery(id+"F0.wireOp",EDGE,"E2");Q11=makeQuery(id+"F0.imprint","IMPRINT",FACE,{"disambiguationData":[TD([[makeQuery(id+"F0.imprint","IMPRINT",EDGE,{"derivedFrom":subQ2}),1.0]])]});}
            var Q12;
            {var subQ0=sQuery(id+"F0.wireOp",EDGE,"E12.5.0");Q12=makeQuery(id+"F0.imprint","IMPRINT",FACE,{"disambiguationData":[TD([[makeQuery(id+"F0.imprint","IMPRINT",EDGE,{"derivedFrom":subQ0}),-1.0]])]});}
            extrude(context, id + "F5", {"entities" : qUnion([Q0, Q1, Q2, Q3, Q4, Q5, Q6, Q7, Q8, Q9, Q10, Q11, Q12]), "depth" : 0.5 * mm});
        }
        {
            var Q0;
            {var subQ5=sQuery(id+"F0.wireOp",EDGE,"E10.4.0");Q0=makeQuery(id+"F0.imprint","IMPRINT",FACE,{"disambiguationData":[TD([[makeQuery(id+"F0.imprint","IMPRINT",EDGE,{"derivedFrom":subQ5}),1.0]])]});}
            var Q1;
            {var subQ6=sQuery(id+"F0.wireOp",EDGE,"E0");Q1=makeQuery(id+"F0.imprint","IMPRINT",FACE,{"disambiguationData":[TD([[makeQuery(id+"F0.imprint","IMPRINT",EDGE,{"derivedFrom":subQ6}),-1.0]])]});}
            var Q2;
            {var subQ0=sQuery(id+"F0.wireOp",EDGE,"E12.3.0");Q2=makeQuery(id+"F0.imprint","IMPRINT",FACE,{"disambiguationData":[TD([[makeQuery(id+"F0.imprint","IMPRINT",EDGE,{"derivedFrom":subQ0}),-1.0]])]});}
            var Q3;
            {var subQ5=sQuery(id+"F0.wireOp",EDGE,"E10.3.0");Q3=makeQuery(id+"F0.imprint","IMPRINT",FACE,{"disambiguationData":[TD([[makeQuery(id+"F0.imprint","IMPRINT",EDGE,{"derivedFrom":subQ5}),1.0]])]});}
            var Q4;
            {var subQ0=sQuery(id+"F0.wireOp",EDGE,"E12.2.0");Q4=makeQuery(id+"F0.imprint","IMPRINT",FACE,{"disambiguationData":[TD([[makeQuery(id+"F0.imprint","IMPRINT",EDGE,{"derivedFrom":subQ0}),-1.0]])]});}
            var Q5;
            {var subQ5=sQuery(id+"F0.wireOp",EDGE,"E10.2.0");Q5=makeQuery(id+"F0.imprint","IMPRINT",FACE,{"disambiguationData":[TD([[makeQuery(id+"F0.imprint","IMPRINT",EDGE,{"derivedFrom":subQ5}),1.0]])]});}
            var Q6;
            {var subQ0=sQuery(id+"F0.wireOp",EDGE,"E12.1.0");Q6=makeQuery(id+"F0.imprint","IMPRINT",FACE,{"disambiguationData":[TD([[makeQuery(id+"F0.imprint","IMPRINT",EDGE,{"derivedFrom":subQ0}),-1.0]])]});}
            var Q7;
            {var subQ5=sQuery(id+"F0.wireOp",EDGE,"E10.1.0");Q7=makeQuery(id+"F0.imprint","IMPRINT",FACE,{"disambiguationData":[TD([[makeQuery(id+"F0.imprint","IMPRINT",EDGE,{"derivedFrom":subQ5}),1.0]])]});}
            var Q8;
            {var subQ1=sQuery(id+"F0.wireOp",EDGE,"E11");Q8=makeQuery(id+"F0.imprint","IMPRINT",FACE,{"disambiguationData":[TD([[makeQuery(id+"F0.imprint","IMPRINT",EDGE,{"derivedFrom":subQ1}),-1.0]])]});}
            var Q9;
            {var subQ2=sQuery(id+"F0.wireOp",EDGE,"E2");Q9=makeQuery(id+"F0.imprint","IMPRINT",FACE,{"disambiguationData":[TD([[makeQuery(id+"F0.imprint","IMPRINT",EDGE,{"derivedFrom":subQ2}),1.0]])]});}
            var Q10;
            {var subQ0=sQuery(id+"F0.wireOp",EDGE,"E12.4.0");Q10=makeQuery(id+"F0.imprint","IMPRINT",FACE,{"disambiguationData":[TD([[makeQuery(id+"F0.imprint","IMPRINT",EDGE,{"derivedFrom":subQ0}),-1.0]])]});}
            extrude(context, id + "F6", {"entities" : qUnion([Q0, Q1, Q2, Q3, Q4, Q5, Q6, Q7, Q8, Q9, Q10]), "depth" : 0.5 * mm});
        }
        {
            var Q0;
            {var subQ6=sQuery(id+"F0.wireOp",EDGE,"E0");Q0=makeQuery(id+"F0.imprint","IMPRINT",FACE,{"disambiguationData":[TD([[makeQuery(id+"F0.imprint","IMPRINT",EDGE,{"derivedFrom":subQ6}),-1.0]])]});}
            var Q1;
            {var subQ5=sQuery(id+"F0.wireOp",EDGE,"E10.3.0");Q1=makeQuery(id+"F0.imprint","IMPRINT",FACE,{"disambiguationData":[TD([[makeQuery(id+"F0.imprint","IMPRINT",EDGE,{"derivedFrom":subQ5}),1.0]])]});}
            var Q2;
            {var subQ0=sQuery(id+"F0.wireOp",EDGE,"E12.2.0");Q2=makeQuery(id+"F0.imprint","IMPRINT",FACE,{"disambiguationData":[TD([[makeQuery(id+"F0.imprint","IMPRINT",EDGE,{"derivedFrom":subQ0}),-1.0]])]});}
            var Q3;
            {var subQ5=sQuery(id+"F0.wireOp",EDGE,"E10.2.0");Q3=makeQuery(id+"F0.imprint","IMPRINT",FACE,{"disambiguationData":[TD([[makeQuery(id+"F0.imprint","IMPRINT",EDGE,{"derivedFrom":subQ5}),1.0]])]});}
            var Q4;
            {var subQ0=sQuery(id+"F0.wireOp",EDGE,"E12.1.0");Q4=makeQuery(id+"F0.imprint","IMPRINT",FACE,{"disambiguationData":[TD([[makeQuery(id+"F0.imprint","IMPRINT",EDGE,{"derivedFrom":subQ0}),-1.0]])]});}
            var Q5;
            {var subQ5=sQuery(id+"F0.wireOp",EDGE,"E10.1.0");Q5=makeQuery(id+"F0.imprint","IMPRINT",FACE,{"disambiguationData":[TD([[makeQuery(id+"F0.imprint","IMPRINT",EDGE,{"derivedFrom":subQ5}),1.0]])]});}
            var Q6;
            {var subQ1=sQuery(id+"F0.wireOp",EDGE,"E11");Q6=makeQuery(id+"F0.imprint","IMPRINT",FACE,{"disambiguationData":[TD([[makeQuery(id+"F0.imprint","IMPRINT",EDGE,{"derivedFrom":subQ1}),-1.0]])]});}
            var Q7;
            {var subQ2=sQuery(id+"F0.wireOp",EDGE,"E2");Q7=makeQuery(id+"F0.imprint","IMPRINT",FACE,{"disambiguationData":[TD([[makeQuery(id+"F0.imprint","IMPRINT",EDGE,{"derivedFrom":subQ2}),1.0]])]});}
            var Q8;
            {var subQ0=sQuery(id+"F0.wireOp",EDGE,"E12.3.0");Q8=makeQuery(id+"F0.imprint","IMPRINT",FACE,{"disambiguationData":[TD([[makeQuery(id+"F0.imprint","IMPRINT",EDGE,{"derivedFrom":subQ0}),-1.0]])]});}
            extrude(context, id + "F7", {"entities" : qUnion([Q0, Q1, Q2, Q3, Q4, Q5, Q6, Q7, Q8]), "depth" : 0.5 * mm});
        }
        {
            var Q0;
            {var subQ6=sQuery(id+"F0.wireOp",EDGE,"E0");Q0=makeQuery(id+"F0.imprint","IMPRINT",FACE,{"disambiguationData":[TD([[makeQuery(id+"F0.imprint","IMPRINT",EDGE,{"derivedFrom":subQ6}),-1.0]])]});}
            var Q1;
            {var subQ5=sQuery(id+"F0.wireOp",EDGE,"E10.2.0");Q1=makeQuery(id+"F0.imprint","IMPRINT",FACE,{"disambiguationData":[TD([[makeQuery(id+"F0.imprint","IMPRINT",EDGE,{"derivedFrom":subQ5}),1.0]])]});}
            var Q2;
            {var subQ0=sQuery(id+"F0.wireOp",EDGE,"E12.1.0");Q2=makeQuery(id+"F0.imprint","IMPRINT",FACE,{"disambiguationData":[TD([[makeQuery(id+"F0.imprint","IMPRINT",EDGE,{"derivedFrom":subQ0}),-1.0]])]});}
            var Q3;
            {var subQ5=sQuery(id+"F0.wireOp",EDGE,"E10.1.0");Q3=makeQuery(id+"F0.imprint","IMPRINT",FACE,{"disambiguationData":[TD([[makeQuery(id+"F0.imprint","IMPRINT",EDGE,{"derivedFrom":subQ5}),1.0]])]});}
            var Q4;
            {var subQ1=sQuery(id+"F0.wireOp",EDGE,"E11");Q4=makeQuery(id+"F0.imprint","IMPRINT",FACE,{"disambiguationData":[TD([[makeQuery(id+"F0.imprint","IMPRINT",EDGE,{"derivedFrom":subQ1}),-1.0]])]});}
            var Q5;
            {var subQ2=sQuery(id+"F0.wireOp",EDGE,"E2");Q5=makeQuery(id+"F0.imprint","IMPRINT",FACE,{"disambiguationData":[TD([[makeQuery(id+"F0.imprint","IMPRINT",EDGE,{"derivedFrom":subQ2}),1.0]])]});}
            var Q6;
            {var subQ0=sQuery(id+"F0.wireOp",EDGE,"E12.2.0");Q6=makeQuery(id+"F0.imprint","IMPRINT",FACE,{"disambiguationData":[TD([[makeQuery(id+"F0.imprint","IMPRINT",EDGE,{"derivedFrom":subQ0}),-1.0]])]});}
            extrude(context, id + "F8", {"entities" : qUnion([Q0, Q1, Q2, Q3, Q4, Q5, Q6]), "depth" : 0.5 * mm});
        }
        {
            var Q0;
            {var subQ6=sQuery(id+"F0.wireOp",EDGE,"E0");Q0=makeQuery(id+"F0.imprint","IMPRINT",FACE,{"disambiguationData":[TD([[makeQuery(id+"F0.imprint","IMPRINT",EDGE,{"derivedFrom":subQ6}),-1.0]])]});}
            var Q1;
            {var subQ5=sQuery(id+"F0.wireOp",EDGE,"E10.1.0");Q1=makeQuery(id+"F0.imprint","IMPRINT",FACE,{"disambiguationData":[TD([[makeQuery(id+"F0.imprint","IMPRINT",EDGE,{"derivedFrom":subQ5}),1.0]])]});}
            var Q2;
            {var subQ1=sQuery(id+"F0.wireOp",EDGE,"E11");Q2=makeQuery(id+"F0.imprint","IMPRINT",FACE,{"disambiguationData":[TD([[makeQuery(id+"F0.imprint","IMPRINT",EDGE,{"derivedFrom":subQ1}),-1.0]])]});}
            var Q3;
            {var subQ2=sQuery(id+"F0.wireOp",EDGE,"E2");Q3=makeQuery(id+"F0.imprint","IMPRINT",FACE,{"disambiguationData":[TD([[makeQuery(id+"F0.imprint","IMPRINT",EDGE,{"derivedFrom":subQ2}),1.0]])]});}
            var Q4;
            {var subQ0=sQuery(id+"F0.wireOp",EDGE,"E12.1.0");Q4=makeQuery(id+"F0.imprint","IMPRINT",FACE,{"disambiguationData":[TD([[makeQuery(id+"F0.imprint","IMPRINT",EDGE,{"derivedFrom":subQ0}),-1.0]])]});}
            extrude(context, id + "F9", {"entities" : qUnion([Q0, Q1, Q2, Q3, Q4]), "depth" : 0.5 * mm});
        }
        {
            var Q0;
            {var subQ6=sQuery(id+"F0.wireOp",EDGE,"E0");Q0=makeQuery(id+"F0.imprint","IMPRINT",FACE,{"disambiguationData":[TD([[makeQuery(id+"F0.imprint","IMPRINT",EDGE,{"derivedFrom":subQ6}),-1.0]])]});}
            var Q1;
            {var subQ2=sQuery(id+"F0.wireOp",EDGE,"E2");Q1=makeQuery(id+"F0.imprint","IMPRINT",FACE,{"disambiguationData":[TD([[makeQuery(id+"F0.imprint","IMPRINT",EDGE,{"derivedFrom":subQ2}),1.0]])]});}
            var Q2;
            {var subQ1=sQuery(id+"F0.wireOp",EDGE,"E11");Q2=makeQuery(id+"F0.imprint","IMPRINT",FACE,{"disambiguationData":[TD([[makeQuery(id+"F0.imprint","IMPRINT",EDGE,{"derivedFrom":subQ1}),-1.0]])]});}
            extrude(context, id + "F10", {"entities" : qUnion([Q0, Q1, Q2]), "depth" : 0.5 * mm});
        }
        {
            var Q0;
            {var subQ5=sQuery(id+"F0.wireOp",EDGE,"E10.1.0");Q0=makeQuery(id+"F0.imprint","IMPRINT",FACE,{"disambiguationData":[TD([[makeQuery(id+"F0.imprint","IMPRINT",EDGE,{"derivedFrom":subQ5}),1.0]])]});}
            var Q1;
            {var subQ0=sQuery(id+"F0.wireOp",EDGE,"E12.1.0");Q1=makeQuery(id+"F0.imprint","IMPRINT",FACE,{"disambiguationData":[TD([[makeQuery(id+"F0.imprint","IMPRINT",EDGE,{"derivedFrom":subQ0}),-1.0]])]});}
            var Q2;
            {var subQ6=sQuery(id+"F0.wireOp",EDGE,"E0");Q2=makeQuery(id+"F0.imprint","IMPRINT",FACE,{"disambiguationData":[TD([[makeQuery(id+"F0.imprint","IMPRINT",EDGE,{"derivedFrom":subQ6}),-1.0]])]});}
            extrude(context, id + "F11", {"entities" : qUnion([Q0, Q1, Q2]), "depth" : 0.5 * mm});
        }
        {
            var Q0;
            {var subQ5=sQuery(id+"F0.wireOp",EDGE,"E10.1.0");Q0=makeQuery(id+"F0.imprint","IMPRINT",FACE,{"disambiguationData":[TD([[makeQuery(id+"F0.imprint","IMPRINT",EDGE,{"derivedFrom":subQ5}),1.0]])]});}
            var Q1;
            {var subQ6=sQuery(id+"F0.wireOp",EDGE,"E0");Q1=makeQuery(id+"F0.imprint","IMPRINT",FACE,{"disambiguationData":[TD([[makeQuery(id+"F0.imprint","IMPRINT",EDGE,{"derivedFrom":subQ6}),-1.0]])]});}
            var Q2;
            {var subQ5=sQuery(id+"F0.wireOp",EDGE,"E10.2.0");Q2=makeQuery(id+"F0.imprint","IMPRINT",FACE,{"disambiguationData":[TD([[makeQuery(id+"F0.imprint","IMPRINT",EDGE,{"derivedFrom":subQ5}),1.0]])]});}
            var Q3;
            {var subQ5=sQuery(id+"F0.wireOp",EDGE,"E10.3.0");Q3=makeQuery(id+"F0.imprint","IMPRINT",FACE,{"disambiguationData":[TD([[makeQuery(id+"F0.imprint","IMPRINT",EDGE,{"derivedFrom":subQ5}),1.0]])]});}
            var Q4;
            {var subQ5=sQuery(id+"F0.wireOp",EDGE,"E10.4.0");Q4=makeQuery(id+"F0.imprint","IMPRINT",FACE,{"disambiguationData":[TD([[makeQuery(id+"F0.imprint","IMPRINT",EDGE,{"derivedFrom":subQ5}),1.0]])]});}
            var Q5;
            {var subQ5=sQuery(id+"F0.wireOp",EDGE,"E10.5.0");Q5=makeQuery(id+"F0.imprint","IMPRINT",FACE,{"disambiguationData":[TD([[makeQuery(id+"F0.imprint","IMPRINT",EDGE,{"derivedFrom":subQ5}),1.0]])]});}
            var Q6;
            {var subQ5=sQuery(id+"F0.wireOp",EDGE,"E10.6.0");Q6=makeQuery(id+"F0.imprint","IMPRINT",FACE,{"disambiguationData":[TD([[makeQuery(id+"F0.imprint","IMPRINT",EDGE,{"derivedFrom":subQ5}),1.0]])]});}
            var Q7;
            {var subQ5=sQuery(id+"F0.wireOp",EDGE,"E10.7.0");Q7=makeQuery(id+"F0.imprint","IMPRINT",FACE,{"disambiguationData":[TD([[makeQuery(id+"F0.imprint","IMPRINT",EDGE,{"derivedFrom":subQ5}),1.0]])]});}
            var Q8;
            {var subQ5=sQuery(id+"F0.wireOp",EDGE,"E10.8.0");Q8=makeQuery(id+"F0.imprint","IMPRINT",FACE,{"disambiguationData":[TD([[makeQuery(id+"F0.imprint","IMPRINT",EDGE,{"derivedFrom":subQ5}),1.0]])]});}
            var Q9;
            {var subQ1=sQuery(id+"F0.wireOp",EDGE,"E10.9.0");Q9=makeQuery(id+"F0.imprint","IMPRINT",FACE,{"disambiguationData":[TD([[makeQuery(id+"F0.imprint","IMPRINT",EDGE,{"derivedFrom":subQ1}),1.0]])]});}
            var Q10;
            {var subQ0=sQuery(id+"F0.wireOp",EDGE,"E12.8.0");Q10=makeQuery(id+"F0.imprint","IMPRINT",FACE,{"disambiguationData":[TD([[makeQuery(id+"F0.imprint","IMPRINT",EDGE,{"derivedFrom":subQ0}),-1.0]])]});}
            var Q11;
            {var subQ0=sQuery(id+"F0.wireOp",EDGE,"E12.7.0");Q11=makeQuery(id+"F0.imprint","IMPRINT",FACE,{"disambiguationData":[TD([[makeQuery(id+"F0.imprint","IMPRINT",EDGE,{"derivedFrom":subQ0}),-1.0]])]});}
            var Q12;
            {var subQ0=sQuery(id+"F0.wireOp",EDGE,"E12.6.0");Q12=makeQuery(id+"F0.imprint","IMPRINT",FACE,{"disambiguationData":[TD([[makeQuery(id+"F0.imprint","IMPRINT",EDGE,{"derivedFrom":subQ0}),-1.0]])]});}
            var Q13;
            {var subQ0=sQuery(id+"F0.wireOp",EDGE,"E12.5.0");Q13=makeQuery(id+"F0.imprint","IMPRINT",FACE,{"disambiguationData":[TD([[makeQuery(id+"F0.imprint","IMPRINT",EDGE,{"derivedFrom":subQ0}),-1.0]])]});}
            var Q14;
            {var subQ0=sQuery(id+"F0.wireOp",EDGE,"E12.4.0");Q14=makeQuery(id+"F0.imprint","IMPRINT",FACE,{"disambiguationData":[TD([[makeQuery(id+"F0.imprint","IMPRINT",EDGE,{"derivedFrom":subQ0}),-1.0]])]});}
            var Q15;
            {var subQ0=sQuery(id+"F0.wireOp",EDGE,"E12.3.0");Q15=makeQuery(id+"F0.imprint","IMPRINT",FACE,{"disambiguationData":[TD([[makeQuery(id+"F0.imprint","IMPRINT",EDGE,{"derivedFrom":subQ0}),-1.0]])]});}
            var Q16;
            {var subQ0=sQuery(id+"F0.wireOp",EDGE,"E12.2.0");Q16=makeQuery(id+"F0.imprint","IMPRINT",FACE,{"disambiguationData":[TD([[makeQuery(id+"F0.imprint","IMPRINT",EDGE,{"derivedFrom":subQ0}),-1.0]])]});}
            var Q17;
            {var subQ0=sQuery(id+"F0.wireOp",EDGE,"E12.1.0");Q17=makeQuery(id+"F0.imprint","IMPRINT",FACE,{"disambiguationData":[TD([[makeQuery(id+"F0.imprint","IMPRINT",EDGE,{"derivedFrom":subQ0}),-1.0]])]});}
            extrude(context, id + "F12", {"entities" : qUnion([Q0, Q1, Q2, Q3, Q4, Q5, Q6, Q7, Q8, Q9, Q10, Q11, Q12, Q13, Q14, Q15, Q16, Q17]), "depth" : 0.5 * mm});
        }
        {
            var Q0;
            Q0=makeQuery(id+"F1.opExtrude","SWEPT_BODY",BODY,{"disambiguationData":[OSD([sQuery(id+"F0.wireOp",EDGE,"E0"),sQuery(id+"F0.wireOp",EDGE,"E1"),sQuery(id+"F0.wireOp",EDGE,"E2"),sQuery(id+"F0.wireOp",EDGE,"E3"),sQuery(id+"F0.wireOp",EDGE,"E4"),sQuery(id+"F0.wireOp",EDGE,"E5"),sQuery(id+"F0.wireOp",EDGE,"E7"),sQuery(id+"F0.wireOp",EDGE,"E8"),sQuery(id+"F0.wireOp",EDGE,"E10.1.0"),sQuery(id+"F0.wireOp",EDGE,"E10.1.1"),sQuery(id+"F0.wireOp",EDGE,"E10.1.2"),sQuery(id+"F0.wireOp",EDGE,"E10.2.0"),sQuery(id+"F0.wireOp",EDGE,"E10.2.1"),sQuery(id+"F0.wireOp",EDGE,"E10.2.2"),sQuery(id+"F0.wireOp",EDGE,"E10.3.0"),sQuery(id+"F0.wireOp",EDGE,"E10.3.1"),sQuery(id+"F0.wireOp",EDGE,"E10.3.2"),sQuery(id+"F0.wireOp",EDGE,"E10.4.0"),sQuery(id+"F0.wireOp",EDGE,"E10.4.1"),sQuery(id+"F0.wireOp",EDGE,"E10.4.2"),sQuery(id+"F0.wireOp",EDGE,"E10.5.0"),sQuery(id+"F0.wireOp",EDGE,"E10.5.1"),sQuery(id+"F0.wireOp",EDGE,"E10.5.2"),sQuery(id+"F0.wireOp",EDGE,"E10.6.0"),sQuery(id+"F0.wireOp",EDGE,"E10.6.1"),sQuery(id+"F0.wireOp",EDGE,"E10.6.2"),sQuery(id+"F0.wireOp",EDGE,"E10.7.0"),sQuery(id+"F0.wireOp",EDGE,"E10.7.1"),sQuery(id+"F0.wireOp",EDGE,"E10.7.2"),sQuery(id+"F0.wireOp",EDGE,"E10.8.0"),sQuery(id+"F0.wireOp",EDGE,"E10.8.1"),sQuery(id+"F0.wireOp",EDGE,"E10.8.2"),sQuery(id+"F0.wireOp",EDGE,"E10.9.0"),sQuery(id+"F0.wireOp",EDGE,"E10.9.1"),sQuery(id+"F0.wireOp",EDGE,"E10.9.2"),sQuery(id+"F0.wireOp",EDGE,"E11"),sQuery(id+"F0.wireOp",EDGE,"E12.1.0"),sQuery(id+"F0.wireOp",EDGE,"E12.2.0"),sQuery(id+"F0.wireOp",EDGE,"E12.3.0"),sQuery(id+"F0.wireOp",EDGE,"E12.4.0"),sQuery(id+"F0.wireOp",EDGE,"E12.5.0"),sQuery(id+"F0.wireOp",EDGE,"E12.6.0"),sQuery(id+"F0.wireOp",EDGE,"E12.7.0"),sQuery(id+"F0.wireOp",EDGE,"E12.8.0"),sQuery(id+"F0.wireOp",EDGE,"E14"),sQuery(id+"F0.wireOp",EDGE,"E16"),sQuery(id+"F0.wireOp",EDGE,"E17"),sQuery(id+"F0.wireOp",EDGE,"E18"),sQuery(id+"F0.wireOp",EDGE,"E19"),sQuery(id+"F0.wireOp",EDGE,"E20.trimOffspring"),sQuery(id+"F0.wireOp",EDGE,"E21.trimOffspring"),sQuery(id+"F0.wireOp",EDGE,"E23"),sQuery(id+"F0.wireOp",EDGE,"E24")])]});
            var Q1;
            Q1=makeQuery(id+"F2.opExtrude","SWEPT_BODY",BODY,{"disambiguationData":[OSD([sQuery(id+"F0.wireOp",EDGE,"E0"),sQuery(id+"F0.wireOp",EDGE,"E1"),sQuery(id+"F0.wireOp",EDGE,"E2"),sQuery(id+"F0.wireOp",EDGE,"E3"),sQuery(id+"F0.wireOp",EDGE,"E4"),sQuery(id+"F0.wireOp",EDGE,"E5"),sQuery(id+"F0.wireOp",EDGE,"E7"),sQuery(id+"F0.wireOp",EDGE,"E8"),sQuery(id+"F0.wireOp",EDGE,"E10.1.0"),sQuery(id+"F0.wireOp",EDGE,"E10.1.1"),sQuery(id+"F0.wireOp",EDGE,"E10.1.2"),sQuery(id+"F0.wireOp",EDGE,"E10.2.0"),sQuery(id+"F0.wireOp",EDGE,"E10.2.1"),sQuery(id+"F0.wireOp",EDGE,"E10.2.2"),sQuery(id+"F0.wireOp",EDGE,"E10.3.0"),sQuery(id+"F0.wireOp",EDGE,"E10.3.1"),sQuery(id+"F0.wireOp",EDGE,"E10.3.2"),sQuery(id+"F0.wireOp",EDGE,"E10.4.0"),sQuery(id+"F0.wireOp",EDGE,"E10.4.1"),sQuery(id+"F0.wireOp",EDGE,"E10.4.2"),sQuery(id+"F0.wireOp",EDGE,"E10.5.0"),sQuery(id+"F0.wireOp",EDGE,"E10.5.1"),sQuery(id+"F0.wireOp",EDGE,"E10.5.2"),sQuery(id+"F0.wireOp",EDGE,"E10.6.0"),sQuery(id+"F0.wireOp",EDGE,"E10.6.1"),sQuery(id+"F0.wireOp",EDGE,"E10.6.2"),sQuery(id+"F0.wireOp",EDGE,"E10.7.0"),sQuery(id+"F0.wireOp",EDGE,"E10.7.1"),sQuery(id+"F0.wireOp",EDGE,"E10.7.2"),sQuery(id+"F0.wireOp",EDGE,"E10.8.0"),sQuery(id+"F0.wireOp",EDGE,"E10.8.1"),sQuery(id+"F0.wireOp",EDGE,"E10.8.2"),sQuery(id+"F0.wireOp",EDGE,"E11"),sQuery(id+"F0.wireOp",EDGE,"E12.1.0"),sQuery(id+"F0.wireOp",EDGE,"E12.2.0"),sQuery(id+"F0.wireOp",EDGE,"E12.3.0"),sQuery(id+"F0.wireOp",EDGE,"E12.4.0"),sQuery(id+"F0.wireOp",EDGE,"E12.5.0"),sQuery(id+"F0.wireOp",EDGE,"E12.6.0"),sQuery(id+"F0.wireOp",EDGE,"E12.7.0"),sQuery(id+"F0.wireOp",EDGE,"E12.8.0"),sQuery(id+"F0.wireOp",EDGE,"E14"),sQuery(id+"F0.wireOp",EDGE,"E16"),sQuery(id+"F0.wireOp",EDGE,"E17"),sQuery(id+"F0.wireOp",EDGE,"E18"),sQuery(id+"F0.wireOp",EDGE,"E19"),sQuery(id+"F0.wireOp",EDGE,"E20.trimOffspring"),sQuery(id+"F0.wireOp",EDGE,"E21.trimOffspring"),sQuery(id+"F0.wireOp",EDGE,"E23"),sQuery(id+"F0.wireOp",EDGE,"E24")])]});
            var Q2;
            Q2=makeQuery(id+"F3.opExtrude","SWEPT_BODY",BODY,{"disambiguationData":[OSD([sQuery(id+"F0.wireOp",EDGE,"E0"),sQuery(id+"F0.wireOp",EDGE,"E1"),sQuery(id+"F0.wireOp",EDGE,"E2"),sQuery(id+"F0.wireOp",EDGE,"E3"),sQuery(id+"F0.wireOp",EDGE,"E4"),sQuery(id+"F0.wireOp",EDGE,"E5"),sQuery(id+"F0.wireOp",EDGE,"E7"),sQuery(id+"F0.wireOp",EDGE,"E8"),sQuery(id+"F0.wireOp",EDGE,"E10.1.0"),sQuery(id+"F0.wireOp",EDGE,"E10.1.1"),sQuery(id+"F0.wireOp",EDGE,"E10.1.2"),sQuery(id+"F0.wireOp",EDGE,"E10.2.0"),sQuery(id+"F0.wireOp",EDGE,"E10.2.1"),sQuery(id+"F0.wireOp",EDGE,"E10.2.2"),sQuery(id+"F0.wireOp",EDGE,"E10.3.0"),sQuery(id+"F0.wireOp",EDGE,"E10.3.1"),sQuery(id+"F0.wireOp",EDGE,"E10.3.2"),sQuery(id+"F0.wireOp",EDGE,"E10.4.0"),sQuery(id+"F0.wireOp",EDGE,"E10.4.1"),sQuery(id+"F0.wireOp",EDGE,"E10.4.2"),sQuery(id+"F0.wireOp",EDGE,"E10.5.0"),sQuery(id+"F0.wireOp",EDGE,"E10.5.1"),sQuery(id+"F0.wireOp",EDGE,"E10.5.2"),sQuery(id+"F0.wireOp",EDGE,"E10.6.0"),sQuery(id+"F0.wireOp",EDGE,"E10.6.1"),sQuery(id+"F0.wireOp",EDGE,"E10.6.2"),sQuery(id+"F0.wireOp",EDGE,"E10.7.0"),sQuery(id+"F0.wireOp",EDGE,"E10.7.1"),sQuery(id+"F0.wireOp",EDGE,"E10.7.2"),sQuery(id+"F0.wireOp",EDGE,"E11"),sQuery(id+"F0.wireOp",EDGE,"E12.1.0"),sQuery(id+"F0.wireOp",EDGE,"E12.2.0"),sQuery(id+"F0.wireOp",EDGE,"E12.3.0"),sQuery(id+"F0.wireOp",EDGE,"E12.4.0"),sQuery(id+"F0.wireOp",EDGE,"E12.5.0"),sQuery(id+"F0.wireOp",EDGE,"E12.6.0"),sQuery(id+"F0.wireOp",EDGE,"E12.7.0"),sQuery(id+"F0.wireOp",EDGE,"E14"),sQuery(id+"F0.wireOp",EDGE,"E16"),sQuery(id+"F0.wireOp",EDGE,"E17"),sQuery(id+"F0.wireOp",EDGE,"E18"),sQuery(id+"F0.wireOp",EDGE,"E19"),sQuery(id+"F0.wireOp",EDGE,"E20.trimOffspring"),sQuery(id+"F0.wireOp",EDGE,"E21.trimOffspring"),sQuery(id+"F0.wireOp",EDGE,"E23"),sQuery(id+"F0.wireOp",EDGE,"E24")])]});
            var Q3;
            Q3=makeQuery(id+"F4.opExtrude","SWEPT_BODY",BODY,{"disambiguationData":[OSD([sQuery(id+"F0.wireOp",EDGE,"E0"),sQuery(id+"F0.wireOp",EDGE,"E1"),sQuery(id+"F0.wireOp",EDGE,"E2"),sQuery(id+"F0.wireOp",EDGE,"E3"),sQuery(id+"F0.wireOp",EDGE,"E4"),sQuery(id+"F0.wireOp",EDGE,"E5"),sQuery(id+"F0.wireOp",EDGE,"E7"),sQuery(id+"F0.wireOp",EDGE,"E8"),sQuery(id+"F0.wireOp",EDGE,"E10.1.0"),sQuery(id+"F0.wireOp",EDGE,"E10.1.1"),sQuery(id+"F0.wireOp",EDGE,"E10.1.2"),sQuery(id+"F0.wireOp",EDGE,"E10.2.0"),sQuery(id+"F0.wireOp",EDGE,"E10.2.1"),sQuery(id+"F0.wireOp",EDGE,"E10.2.2"),sQuery(id+"F0.wireOp",EDGE,"E10.3.0"),sQuery(id+"F0.wireOp",EDGE,"E10.3.1"),sQuery(id+"F0.wireOp",EDGE,"E10.3.2"),sQuery(id+"F0.wireOp",EDGE,"E10.4.0"),sQuery(id+"F0.wireOp",EDGE,"E10.4.1"),sQuery(id+"F0.wireOp",EDGE,"E10.4.2"),sQuery(id+"F0.wireOp",EDGE,"E10.5.0"),sQuery(id+"F0.wireOp",EDGE,"E10.5.1"),sQuery(id+"F0.wireOp",EDGE,"E10.5.2"),sQuery(id+"F0.wireOp",EDGE,"E10.6.0"),sQuery(id+"F0.wireOp",EDGE,"E10.6.1"),sQuery(id+"F0.wireOp",EDGE,"E10.6.2"),sQuery(id+"F0.wireOp",EDGE,"E11"),sQuery(id+"F0.wireOp",EDGE,"E12.1.0"),sQuery(id+"F0.wireOp",EDGE,"E12.2.0"),sQuery(id+"F0.wireOp",EDGE,"E12.3.0"),sQuery(id+"F0.wireOp",EDGE,"E12.4.0"),sQuery(id+"F0.wireOp",EDGE,"E12.5.0"),sQuery(id+"F0.wireOp",EDGE,"E12.6.0"),sQuery(id+"F0.wireOp",EDGE,"E14"),sQuery(id+"F0.wireOp",EDGE,"E16"),sQuery(id+"F0.wireOp",EDGE,"E17"),sQuery(id+"F0.wireOp",EDGE,"E18"),sQuery(id+"F0.wireOp",EDGE,"E19"),sQuery(id+"F0.wireOp",EDGE,"E20.trimOffspring"),sQuery(id+"F0.wireOp",EDGE,"E21.trimOffspring"),sQuery(id+"F0.wireOp",EDGE,"E23"),sQuery(id+"F0.wireOp",EDGE,"E24")])]});
            var Q4;
            Q4=makeQuery(id+"F5.opExtrude","SWEPT_BODY",BODY,{"disambiguationData":[OSD([sQuery(id+"F0.wireOp",EDGE,"E0"),sQuery(id+"F0.wireOp",EDGE,"E1"),sQuery(id+"F0.wireOp",EDGE,"E2"),sQuery(id+"F0.wireOp",EDGE,"E3"),sQuery(id+"F0.wireOp",EDGE,"E4"),sQuery(id+"F0.wireOp",EDGE,"E5"),sQuery(id+"F0.wireOp",EDGE,"E7"),sQuery(id+"F0.wireOp",EDGE,"E8"),sQuery(id+"F0.wireOp",EDGE,"E10.1.0"),sQuery(id+"F0.wireOp",EDGE,"E10.1.1"),sQuery(id+"F0.wireOp",EDGE,"E10.1.2"),sQuery(id+"F0.wireOp",EDGE,"E10.2.0"),sQuery(id+"F0.wireOp",EDGE,"E10.2.1"),sQuery(id+"F0.wireOp",EDGE,"E10.2.2"),sQuery(id+"F0.wireOp",EDGE,"E10.3.0"),sQuery(id+"F0.wireOp",EDGE,"E10.3.1"),sQuery(id+"F0.wireOp",EDGE,"E10.3.2"),sQuery(id+"F0.wireOp",EDGE,"E10.4.0"),sQuery(id+"F0.wireOp",EDGE,"E10.4.1"),sQuery(id+"F0.wireOp",EDGE,"E10.4.2"),sQuery(id+"F0.wireOp",EDGE,"E10.5.0"),sQuery(id+"F0.wireOp",EDGE,"E10.5.1"),sQuery(id+"F0.wireOp",EDGE,"E10.5.2"),sQuery(id+"F0.wireOp",EDGE,"E11"),sQuery(id+"F0.wireOp",EDGE,"E12.1.0"),sQuery(id+"F0.wireOp",EDGE,"E12.2.0"),sQuery(id+"F0.wireOp",EDGE,"E12.3.0"),sQuery(id+"F0.wireOp",EDGE,"E12.4.0"),sQuery(id+"F0.wireOp",EDGE,"E12.5.0"),sQuery(id+"F0.wireOp",EDGE,"E14"),sQuery(id+"F0.wireOp",EDGE,"E16"),sQuery(id+"F0.wireOp",EDGE,"E17"),sQuery(id+"F0.wireOp",EDGE,"E18"),sQuery(id+"F0.wireOp",EDGE,"E19"),sQuery(id+"F0.wireOp",EDGE,"E20.trimOffspring"),sQuery(id+"F0.wireOp",EDGE,"E21.trimOffspring"),sQuery(id+"F0.wireOp",EDGE,"E23"),sQuery(id+"F0.wireOp",EDGE,"E24")])]});
            var Q5;
            Q5=makeQuery(id+"F6.opExtrude","SWEPT_BODY",BODY,{"disambiguationData":[OSD([sQuery(id+"F0.wireOp",EDGE,"E0"),sQuery(id+"F0.wireOp",EDGE,"E1"),sQuery(id+"F0.wireOp",EDGE,"E2"),sQuery(id+"F0.wireOp",EDGE,"E3"),sQuery(id+"F0.wireOp",EDGE,"E4"),sQuery(id+"F0.wireOp",EDGE,"E5"),sQuery(id+"F0.wireOp",EDGE,"E7"),sQuery(id+"F0.wireOp",EDGE,"E8"),sQuery(id+"F0.wireOp",EDGE,"E10.1.0"),sQuery(id+"F0.wireOp",EDGE,"E10.1.1"),sQuery(id+"F0.wireOp",EDGE,"E10.1.2"),sQuery(id+"F0.wireOp",EDGE,"E10.2.0"),sQuery(id+"F0.wireOp",EDGE,"E10.2.1"),sQuery(id+"F0.wireOp",EDGE,"E10.2.2"),sQuery(id+"F0.wireOp",EDGE,"E10.3.0"),sQuery(id+"F0.wireOp",EDGE,"E10.3.1"),sQuery(id+"F0.wireOp",EDGE,"E10.3.2"),sQuery(id+"F0.wireOp",EDGE,"E10.4.0"),sQuery(id+"F0.wireOp",EDGE,"E10.4.1"),sQuery(id+"F0.wireOp",EDGE,"E10.4.2"),sQuery(id+"F0.wireOp",EDGE,"E11"),sQuery(id+"F0.wireOp",EDGE,"E12.1.0"),sQuery(id+"F0.wireOp",EDGE,"E12.2.0"),sQuery(id+"F0.wireOp",EDGE,"E12.3.0"),sQuery(id+"F0.wireOp",EDGE,"E12.4.0"),sQuery(id+"F0.wireOp",EDGE,"E14"),sQuery(id+"F0.wireOp",EDGE,"E16"),sQuery(id+"F0.wireOp",EDGE,"E17"),sQuery(id+"F0.wireOp",EDGE,"E18"),sQuery(id+"F0.wireOp",EDGE,"E19"),sQuery(id+"F0.wireOp",EDGE,"E20.trimOffspring"),sQuery(id+"F0.wireOp",EDGE,"E21.trimOffspring"),sQuery(id+"F0.wireOp",EDGE,"E23"),sQuery(id+"F0.wireOp",EDGE,"E24")])]});
            var Q6;
            Q6=makeQuery(id+"F7.opExtrude","SWEPT_BODY",BODY,{"disambiguationData":[OSD([sQuery(id+"F0.wireOp",EDGE,"E0"),sQuery(id+"F0.wireOp",EDGE,"E1"),sQuery(id+"F0.wireOp",EDGE,"E2"),sQuery(id+"F0.wireOp",EDGE,"E3"),sQuery(id+"F0.wireOp",EDGE,"E4"),sQuery(id+"F0.wireOp",EDGE,"E5"),sQuery(id+"F0.wireOp",EDGE,"E7"),sQuery(id+"F0.wireOp",EDGE,"E8"),sQuery(id+"F0.wireOp",EDGE,"E10.1.0"),sQuery(id+"F0.wireOp",EDGE,"E10.1.1"),sQuery(id+"F0.wireOp",EDGE,"E10.1.2"),sQuery(id+"F0.wireOp",EDGE,"E10.2.0"),sQuery(id+"F0.wireOp",EDGE,"E10.2.1"),sQuery(id+"F0.wireOp",EDGE,"E10.2.2"),sQuery(id+"F0.wireOp",EDGE,"E10.3.0"),sQuery(id+"F0.wireOp",EDGE,"E10.3.1"),sQuery(id+"F0.wireOp",EDGE,"E10.3.2"),sQuery(id+"F0.wireOp",EDGE,"E11"),sQuery(id+"F0.wireOp",EDGE,"E12.1.0"),sQuery(id+"F0.wireOp",EDGE,"E12.2.0"),sQuery(id+"F0.wireOp",EDGE,"E12.3.0"),sQuery(id+"F0.wireOp",EDGE,"E14"),sQuery(id+"F0.wireOp",EDGE,"E16"),sQuery(id+"F0.wireOp",EDGE,"E17"),sQuery(id+"F0.wireOp",EDGE,"E18"),sQuery(id+"F0.wireOp",EDGE,"E19"),sQuery(id+"F0.wireOp",EDGE,"E20.trimOffspring"),sQuery(id+"F0.wireOp",EDGE,"E21.trimOffspring"),sQuery(id+"F0.wireOp",EDGE,"E23"),sQuery(id+"F0.wireOp",EDGE,"E24")])]});
            var Q7;
            Q7=makeQuery(id+"F8.opExtrude","SWEPT_BODY",BODY,{"disambiguationData":[OSD([sQuery(id+"F0.wireOp",EDGE,"E0"),sQuery(id+"F0.wireOp",EDGE,"E1"),sQuery(id+"F0.wireOp",EDGE,"E2"),sQuery(id+"F0.wireOp",EDGE,"E3"),sQuery(id+"F0.wireOp",EDGE,"E4"),sQuery(id+"F0.wireOp",EDGE,"E5"),sQuery(id+"F0.wireOp",EDGE,"E7"),sQuery(id+"F0.wireOp",EDGE,"E8"),sQuery(id+"F0.wireOp",EDGE,"E10.1.0"),sQuery(id+"F0.wireOp",EDGE,"E10.1.1"),sQuery(id+"F0.wireOp",EDGE,"E10.1.2"),sQuery(id+"F0.wireOp",EDGE,"E10.2.0"),sQuery(id+"F0.wireOp",EDGE,"E10.2.1"),sQuery(id+"F0.wireOp",EDGE,"E10.2.2"),sQuery(id+"F0.wireOp",EDGE,"E11"),sQuery(id+"F0.wireOp",EDGE,"E12.1.0"),sQuery(id+"F0.wireOp",EDGE,"E12.2.0"),sQuery(id+"F0.wireOp",EDGE,"E14"),sQuery(id+"F0.wireOp",EDGE,"E16"),sQuery(id+"F0.wireOp",EDGE,"E17"),sQuery(id+"F0.wireOp",EDGE,"E18"),sQuery(id+"F0.wireOp",EDGE,"E19"),sQuery(id+"F0.wireOp",EDGE,"E20.trimOffspring"),sQuery(id+"F0.wireOp",EDGE,"E21.trimOffspring"),sQuery(id+"F0.wireOp",EDGE,"E23"),sQuery(id+"F0.wireOp",EDGE,"E24")])]});
            var Q8;
            Q8=makeQuery(id+"F9.opExtrude","SWEPT_BODY",BODY,{"disambiguationData":[OSD([sQuery(id+"F0.wireOp",EDGE,"E0"),sQuery(id+"F0.wireOp",EDGE,"E1"),sQuery(id+"F0.wireOp",EDGE,"E2"),sQuery(id+"F0.wireOp",EDGE,"E3"),sQuery(id+"F0.wireOp",EDGE,"E4"),sQuery(id+"F0.wireOp",EDGE,"E5"),sQuery(id+"F0.wireOp",EDGE,"E7"),sQuery(id+"F0.wireOp",EDGE,"E8"),sQuery(id+"F0.wireOp",EDGE,"E10.1.0"),sQuery(id+"F0.wireOp",EDGE,"E10.1.1"),sQuery(id+"F0.wireOp",EDGE,"E10.1.2"),sQuery(id+"F0.wireOp",EDGE,"E11"),sQuery(id+"F0.wireOp",EDGE,"E12.1.0"),sQuery(id+"F0.wireOp",EDGE,"E14"),sQuery(id+"F0.wireOp",EDGE,"E16"),sQuery(id+"F0.wireOp",EDGE,"E17"),sQuery(id+"F0.wireOp",EDGE,"E18"),sQuery(id+"F0.wireOp",EDGE,"E19"),sQuery(id+"F0.wireOp",EDGE,"E20.trimOffspring"),sQuery(id+"F0.wireOp",EDGE,"E21.trimOffspring"),sQuery(id+"F0.wireOp",EDGE,"E23"),sQuery(id+"F0.wireOp",EDGE,"E24")])]});
            var Q9;
            Q9=makeQuery(id+"F10.opExtrude","SWEPT_BODY",BODY,{"disambiguationData":[OSD([sQuery(id+"F0.wireOp",EDGE,"E0"),sQuery(id+"F0.wireOp",EDGE,"E1"),sQuery(id+"F0.wireOp",EDGE,"E2"),sQuery(id+"F0.wireOp",EDGE,"E3"),sQuery(id+"F0.wireOp",EDGE,"E4"),sQuery(id+"F0.wireOp",EDGE,"E5"),sQuery(id+"F0.wireOp",EDGE,"E7"),sQuery(id+"F0.wireOp",EDGE,"E8"),sQuery(id+"F0.wireOp",EDGE,"E11"),sQuery(id+"F0.wireOp",EDGE,"E14"),sQuery(id+"F0.wireOp",EDGE,"E16"),sQuery(id+"F0.wireOp",EDGE,"E17"),sQuery(id+"F0.wireOp",EDGE,"E18"),sQuery(id+"F0.wireOp",EDGE,"E19"),sQuery(id+"F0.wireOp",EDGE,"E20.trimOffspring"),sQuery(id+"F0.wireOp",EDGE,"E21.trimOffspring"),sQuery(id+"F0.wireOp",EDGE,"E23"),sQuery(id+"F0.wireOp",EDGE,"E24")])]});
            var Q10;
            Q10=makeQuery(id+"F11.opExtrude","SWEPT_BODY",BODY,{"disambiguationData":[OSD([sQuery(id+"F0.wireOp",EDGE,"E0"),sQuery(id+"F0.wireOp",EDGE,"E1"),sQuery(id+"F0.wireOp",EDGE,"E3"),sQuery(id+"F0.wireOp",EDGE,"E4"),sQuery(id+"F0.wireOp",EDGE,"E5"),sQuery(id+"F0.wireOp",EDGE,"E10.1.0"),sQuery(id+"F0.wireOp",EDGE,"E10.1.1"),sQuery(id+"F0.wireOp",EDGE,"E10.1.2"),sQuery(id+"F0.wireOp",EDGE,"E12.1.0"),sQuery(id+"F0.wireOp",EDGE,"E14"),sQuery(id+"F0.wireOp",EDGE,"E16"),sQuery(id+"F0.wireOp",EDGE,"E17"),sQuery(id+"F0.wireOp",EDGE,"E18"),sQuery(id+"F0.wireOp",EDGE,"E19"),sQuery(id+"F0.wireOp",EDGE,"E20.trimOffspring"),sQuery(id+"F0.wireOp",EDGE,"E21.trimOffspring"),sQuery(id+"F0.wireOp",EDGE,"E23"),sQuery(id+"F0.wireOp",EDGE,"E24")])]});
            var Q11;
            Q11=makeQuery(id+"F12.opExtrude","SWEPT_BODY",BODY,{"disambiguationData":[OSD([sQuery(id+"F0.wireOp",EDGE,"E0"),sQuery(id+"F0.wireOp",EDGE,"E1"),sQuery(id+"F0.wireOp",EDGE,"E3"),sQuery(id+"F0.wireOp",EDGE,"E4"),sQuery(id+"F0.wireOp",EDGE,"E5"),sQuery(id+"F0.wireOp",EDGE,"E10.1.0"),sQuery(id+"F0.wireOp",EDGE,"E10.1.1"),sQuery(id+"F0.wireOp",EDGE,"E10.1.2"),sQuery(id+"F0.wireOp",EDGE,"E10.2.0"),sQuery(id+"F0.wireOp",EDGE,"E10.2.1"),sQuery(id+"F0.wireOp",EDGE,"E10.2.2"),sQuery(id+"F0.wireOp",EDGE,"E10.3.0"),sQuery(id+"F0.wireOp",EDGE,"E10.3.1"),sQuery(id+"F0.wireOp",EDGE,"E10.3.2"),sQuery(id+"F0.wireOp",EDGE,"E10.4.0"),sQuery(id+"F0.wireOp",EDGE,"E10.4.1"),sQuery(id+"F0.wireOp",EDGE,"E10.4.2"),sQuery(id+"F0.wireOp",EDGE,"E10.5.0"),sQuery(id+"F0.wireOp",EDGE,"E10.5.1"),sQuery(id+"F0.wireOp",EDGE,"E10.5.2"),sQuery(id+"F0.wireOp",EDGE,"E10.6.0"),sQuery(id+"F0.wireOp",EDGE,"E10.6.1"),sQuery(id+"F0.wireOp",EDGE,"E10.6.2"),sQuery(id+"F0.wireOp",EDGE,"E10.7.0"),sQuery(id+"F0.wireOp",EDGE,"E10.7.1"),sQuery(id+"F0.wireOp",EDGE,"E10.7.2"),sQuery(id+"F0.wireOp",EDGE,"E10.8.0"),sQuery(id+"F0.wireOp",EDGE,"E10.8.1"),sQuery(id+"F0.wireOp",EDGE,"E10.8.2"),sQuery(id+"F0.wireOp",EDGE,"E10.9.0"),sQuery(id+"F0.wireOp",EDGE,"E10.9.1"),sQuery(id+"F0.wireOp",EDGE,"E10.9.2"),sQuery(id+"F0.wireOp",EDGE,"E12.1.0"),sQuery(id+"F0.wireOp",EDGE,"E12.2.0"),sQuery(id+"F0.wireOp",EDGE,"E12.3.0"),sQuery(id+"F0.wireOp",EDGE,"E12.4.0"),sQuery(id+"F0.wireOp",EDGE,"E12.5.0"),sQuery(id+"F0.wireOp",EDGE,"E12.6.0"),sQuery(id+"F0.wireOp",EDGE,"E12.7.0"),sQuery(id+"F0.wireOp",EDGE,"E12.8.0"),sQuery(id+"F0.wireOp",EDGE,"E14"),sQuery(id+"F0.wireOp",EDGE,"E16"),sQuery(id+"F0.wireOp",EDGE,"E17"),sQuery(id+"F0.wireOp",EDGE,"E18"),sQuery(id+"F0.wireOp",EDGE,"E19"),sQuery(id+"F0.wireOp",EDGE,"E20.trimOffspring"),sQuery(id+"F0.wireOp",EDGE,"E21.trimOffspring"),sQuery(id+"F0.wireOp",EDGE,"E23"),sQuery(id+"F0.wireOp",EDGE,"E24")])]});
            var Q12;
            Q12=qCreatedBy(makeId("Origin.pointOp"),VERTEX);
            transform(context, id + "F13", {"entities" : qUnion([Q0, Q1, Q2, Q3, Q4, Q5, Q6, Q7, Q8, Q9, Q10, Q11]), "transformType" : TransformType.SCALE_UNIFORMLY, "scale" : 3, "makeCopy" : false, "scalePoint" : qUnion([Q12])});
        }
    });
